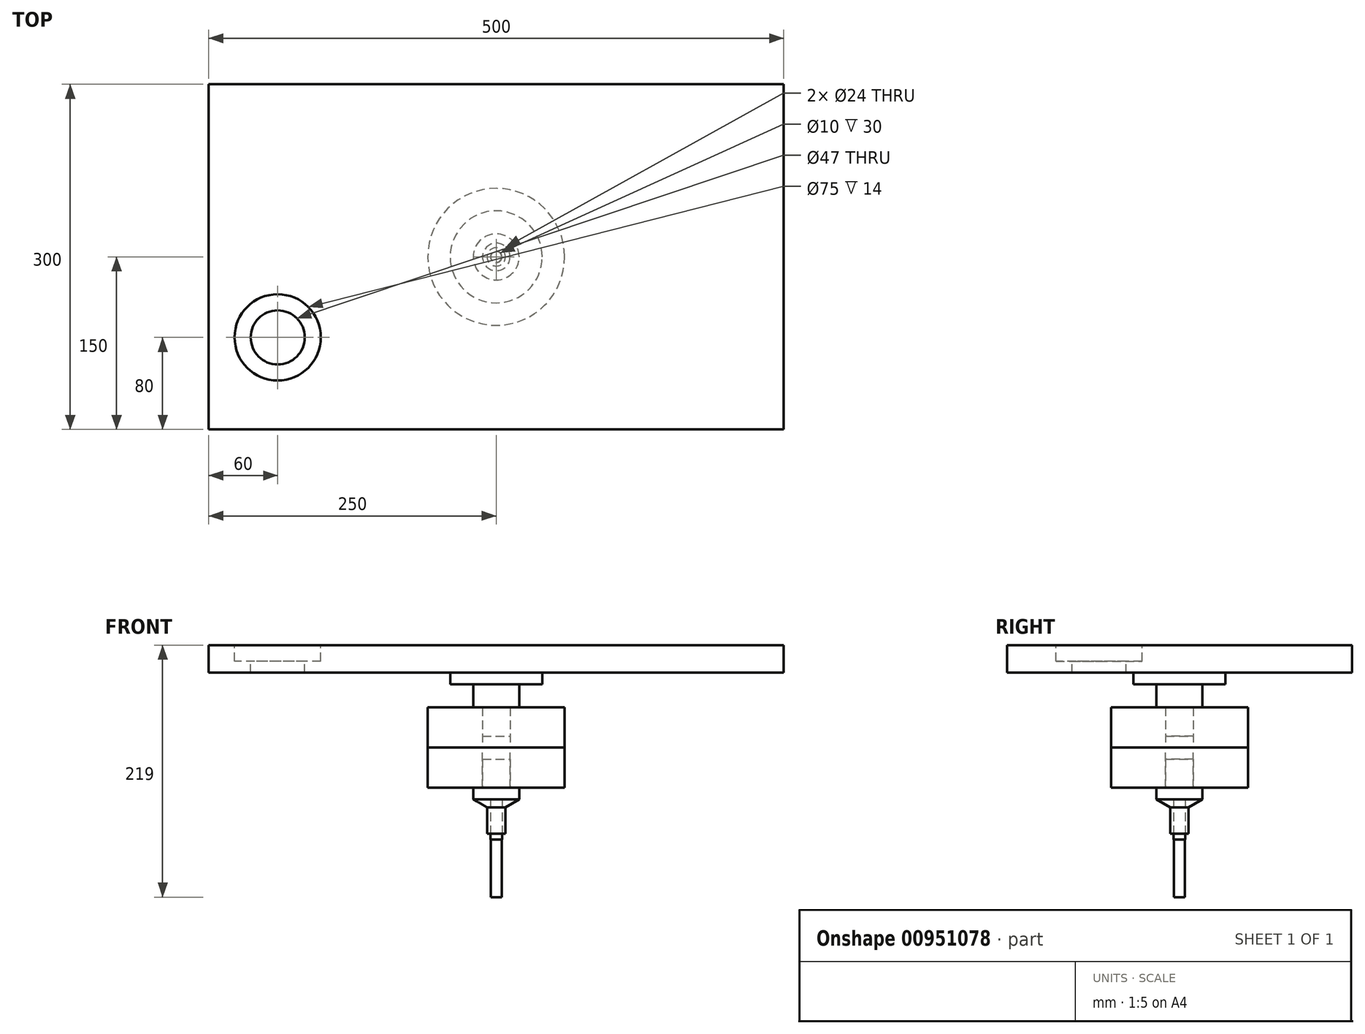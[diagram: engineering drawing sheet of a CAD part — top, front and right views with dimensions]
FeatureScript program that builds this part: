
annotation { "Feature Type Name" : "Feature", "Feature Type Description" : "" }
export const myFeature = defineFeature(function(context is Context, id is Id, definition is map)
    precondition{}
    {
        {
            var Q0;
            Q0=qCreatedBy(makeId("Top.planeOp"),FACE);
            var sketch = newSketch(context, id + "F0", { "sketchPlane" : qUnion([Q0])});
            skLineSegment(sketch, "E0.bottom", {"start": v(250, 150) * mm, "end": v(-250, 150) * mm});
            skLineSegment(sketch, "E0.top", {"start": v(250, -150) * mm, "end": v(-250, -150) * mm});
            skLineSegment(sketch, "E0.left", {"start": v(250, 150) * mm, "end": v(250, -150) * mm});
            skLineSegment(sketch, "E0.right", {"start": v(-250, 150) * mm, "end": v(-250, -150) * mm});
            skPoint(sketch, "E0.middle", {"position": v(0, 0) * mm});
            skSolve(sketch);
        }
        {
            var Q0;
            Q0=makeQuery(id+"F0.imprint","IMPRINT",FACE,{"disambiguationData":[TD([[makeQuery(id+"F0.imprint","IMPRINT",EDGE,{"derivedFrom":sQuery(id+"F0.wireOp",EDGE,"E0.bottom")}),1.0]])]});
            var Q1;
            Q1=makeQuery(id+"F0.imprint","IMPRINT",FACE,{"disambiguationData":[TD([[makeQuery(id+"F0.imprint","IMPRINT",EDGE,{"derivedFrom":sQuery(id+"F0.wireOp",EDGE,"58def0f7-d9c0-4334-95c1-cc013ec1d39d.1.0.0")}),1.0]])]});
            var Q2;
            Q2=makeQuery(id+"F0.imprint","IMPRINT",FACE,{"disambiguationData":[TD([[makeQuery(id+"F0.imprint","IMPRINT",EDGE,{"derivedFrom":sQuery(id+"F0.wireOp",EDGE,"58def0f7-d9c0-4334-95c1-cc013ec1d39d.1.0.0")}),-1.0]])]});
            var Q3;
            Q3=makeQuery(id+"F0.imprint","IMPRINT",FACE,{"disambiguationData":[TD([[makeQuery(id+"F0.imprint","IMPRINT",EDGE,{"derivedFrom":sQuery(id+"F0.wireOp",EDGE,"58def0f7-d9c0-4334-95c1-cc013ec1d39d.1.1.0")}),-1.0]])]});
            var Q4;
            Q4=makeQuery(id+"F0.imprint","IMPRINT",FACE,{"disambiguationData":[TD([[makeQuery(id+"F0.imprint","IMPRINT",EDGE,{"derivedFrom":sQuery(id+"F0.wireOp",EDGE,"58def0f7-d9c0-4334-95c1-cc013ec1d39d.1.1.0")}),1.0]])]});
            var Q5;
            Q5=makeQuery(id+"F0.imprint","IMPRINT",FACE,{"disambiguationData":[TD([[makeQuery(id+"F0.imprint","IMPRINT",EDGE,{"derivedFrom":sQuery(id+"F0.wireOp",EDGE,"58def0f7-d9c0-4334-95c1-cc013ec1d39d.0.1.0")}),-1.0]])]});
            var Q6;
            Q6=makeQuery(id+"F0.imprint","IMPRINT",FACE,{"disambiguationData":[TD([[makeQuery(id+"F0.imprint","IMPRINT",EDGE,{"derivedFrom":sQuery(id+"F0.wireOp",EDGE,"58def0f7-d9c0-4334-95c1-cc013ec1d39d.0.1.0")}),1.0]])]});
            var Q7;
            Q7=makeQuery(id+"F0.imprint","IMPRINT",FACE,{"disambiguationData":[TD([[makeQuery(id+"F0.imprint","IMPRINT",EDGE,{"derivedFrom":sQuery(id+"F0.wireOp",EDGE,"4IipATZv-LVdL-YkI8-DpBN-fSkK8KW6vcjz")}),1.0]])]});
            var Q8;
            Q8=makeQuery(id+"F0.imprint","IMPRINT",FACE,{"disambiguationData":[TD([[makeQuery(id+"F0.imprint","IMPRINT",EDGE,{"derivedFrom":sQuery(id+"F0.wireOp",EDGE,"YpDaPiLN-B9xz-3bgj-5HSM-HLz1pKYE0Ii8")}),1.0]])]});
            extrude(context, id + "F1", {"entities" : qUnion([Q0, Q1, Q2, Q3, Q4, Q5, Q6, Q7, Q8]), "depth" : 24 * mm, "offsetDistance" : 25 * mm});
        }
        {
            var Q0;
            Q0=makeQuery(id+"F1.opExtrude","CAP_FACE",FACE,{"disambiguationData":[OSD([sQuery(id+"F0.wireOp",EDGE,"E0.bottom"),sQuery(id+"F0.wireOp",EDGE,"E0.top"),sQuery(id+"F0.wireOp",EDGE,"E0.left"),sQuery(id+"F0.wireOp",EDGE,"E0.right")])],"isStart":false});
            var sketch = newSketch(context, id + "F2", { "sketchPlane" : qUnion([Q0])});
            skCircle(sketch, "E1", {"center": v(-190, -70) * mm, "radius": 37.5 * mm});
            skCircle(sketch, "E2", {"center": v(-190, -70) * mm, "radius": 23.5 * mm});
            skSolve(sketch);
        }
        {
            var Q0;
            Q0=makeQuery(id+"F2.imprint","IMPRINT",FACE,{"disambiguationData":[TD([[makeQuery(id+"F2.imprint","IMPRINT",EDGE,{"derivedFrom":sQuery(id+"F2.wireOp",EDGE,"E2")}),1.0]])]});
            extrude(context, id + "F3", {"entities" : qUnion([Q0]), "operationType" : NewBodyOperationType.REMOVE, "endBound" : BoundingType.THROUGH_ALL, "oppositeDirection" : true, "depth" : 25 * mm, "offsetDistance" : 25 * mm});
        }
        {
            var Q0;
            Q0=makeQuery(id+"F2.imprint","IMPRINT",FACE,{"disambiguationData":[TD([[makeQuery(id+"F2.imprint","IMPRINT",EDGE,{"derivedFrom":sQuery(id+"F2.wireOp",EDGE,"E1")}),1.0]])]});
            extrude(context, id + "F4", {"entities" : qUnion([Q0]), "operationType" : NewBodyOperationType.REMOVE, "oppositeDirection" : true, "depth" : 14 * mm, "offsetDistance" : 25 * mm});
        }
        {
            var Q0;
            Q0=qCreatedBy(makeId("Front.planeOp"),FACE);
            var sketch = newSketch(context, id + "F5", { "sketchPlane" : qUnion([Q0])});
            skLineSegment(sketch, "E3", {"start": v(0, -55) * mm, "end": v(0, 0) * mm});
            skLineSegment(sketch, "E4", {"start": v(0, 0) * mm, "end": v(40, 0) * mm});
            skLineSegment(sketch, "E5", {"start": v(40, 0) * mm, "end": v(40, -10) * mm});
            skLineSegment(sketch, "E6", {"start": v(12, -30) * mm, "end": v(12, -55) * mm});
            skLineSegment(sketch, "E7", {"start": v(12, -55) * mm, "end": v(0, -55) * mm});
            skLineSegment(sketch, "E8", {"start": v(12, -30) * mm, "end": v(20, -30) * mm});
            skLineSegment(sketch, "E9", {"start": v(20, -30) * mm, "end": v(20, -10) * mm});
            skLineSegment(sketch, "E10", {"start": v(20, -10) * mm, "end": v(40, -10) * mm});
            skLineSegment(sketch, "E11.MirrorCS", {"start": v(-12, -30) * mm, "end": v(-12, -55) * mm, "construction": true});
            skLineSegment(sketch, "E12.MirrorCS", {"start": v(-20, -30) * mm, "end": v(-20, -10) * mm, "construction": true});
            skLineSegment(sketch, "E13.MirrorCS", {"start": v(-40, 0) * mm, "end": v(-40, -10) * mm, "construction": true});
            skLineSegment(sketch, "E14", {"start": v(20, -30) * mm, "end": v(59.5, -30) * mm});
            skLineSegment(sketch, "E15", {"start": v(59.5, -30) * mm, "end": v(59.5, -65) * mm});
            skLineSegment(sketch, "E16", {"start": v(59.5, -65) * mm, "end": v(12, -65) * mm});
            skLineSegment(sketch, "E17", {"start": v(12, -65) * mm, "end": v(12, -55) * mm});
            skLineSegment(sketch, "E18.MirrorCS", {"start": v(-59.5, -30) * mm, "end": v(-59.5, -65) * mm, "construction": true});
            skLineSegment(sketch, "E19", {"start": v(0, -75) * mm, "end": v(12, -75) * mm});
            skLineSegment(sketch, "E20", {"start": v(12, -75) * mm, "end": v(12, -100) * mm});
            skLineSegment(sketch, "E21", {"start": v(12, -100) * mm, "end": v(20, -100) * mm});
            skLineSegment(sketch, "E22", {"start": v(20, -100) * mm, "end": v(20, -110) * mm});
            skLineSegment(sketch, "E23", {"start": v(20, -110) * mm, "end": v(8, -110) * mm});
            skLineSegment(sketch, "E24", {"start": v(8, -110) * mm, "end": v(8, -140) * mm});
            skLineSegment(sketch, "E25", {"start": v(8, -140) * mm, "end": v(5, -140) * mm});
            skLineSegment(sketch, "E26", {"start": v(5, -140) * mm, "end": v(5, -110) * mm});
            skLineSegment(sketch, "E27", {"start": v(5, -110) * mm, "end": v(0, -110) * mm});
            skLineSegment(sketch, "E28", {"start": v(0, -110) * mm, "end": v(0, -75) * mm});
            skLineSegment(sketch, "E29.MirrorCS", {"start": v(-5, -140) * mm, "end": v(-5, -110) * mm, "construction": true});
            skLineSegment(sketch, "E30.MirrorCS", {"start": v(-8, -110) * mm, "end": v(-8, -140) * mm, "construction": true});
            skLineSegment(sketch, "E31", {"start": v(5, -140) * mm, "end": v(5, -145) * mm});
            skLineSegment(sketch, "E32", {"start": v(5, -145) * mm, "end": v(4.75, -145) * mm});
            skLineSegment(sketch, "E33", {"start": v(4.75, -145) * mm, "end": v(4.75, -195) * mm});
            skLineSegment(sketch, "E34", {"start": v(4.75, -195) * mm, "end": v(0, -195) * mm});
            skLineSegment(sketch, "E35", {"start": v(0, -195) * mm, "end": v(0, -110) * mm});
            skLineSegment(sketch, "E36.MirrorCS", {"start": v(-4.75, -145) * mm, "end": v(-4.75, -195) * mm, "construction": true});
            skLineSegment(sketch, "E37", {"start": v(20, -110) * mm, "end": v(8, -116.93) * mm});
            skSolve(sketch);
        }
        {
            var Q0;
            Q0=makeQuery(id+"F5.imprint","IMPRINT",FACE,{"disambiguationData":[TD([[makeQuery(id+"F5.imprint","IMPRINT",EDGE,{"derivedFrom":sQuery(id+"F5.wireOp",EDGE,"E3")}),-1.0]])]});
            var Q1;
            Q1=sQuery(id+"F5.wireOp",EDGE,"E3");
            revolve(context, id + "F6", {"surfaceOperationType" : NewSurfaceOperationType.NEW, "entities" : qUnion([Q0]), "axis" : qUnion([Q1]), "revolveType" : RevolveType.FULL});
        }
        {
            var Q0;
            Q0=makeQuery(id+"F5.imprint","IMPRINT",FACE,{"disambiguationData":[TD([[makeQuery(id+"F5.imprint","IMPRINT",EDGE,{"derivedFrom":sQuery(id+"F5.wireOp",EDGE,"E6")}),1.0]])]});
            var Q1;
            Q1=sQuery(id+"F5.wireOp",EDGE,"E3");
            revolve(context, id + "F7", {"surfaceOperationType" : NewSurfaceOperationType.NEW, "entities" : qUnion([Q0]), "axis" : qUnion([Q1]), "revolveType" : RevolveType.FULL});
        }
        {
            var Q0;
            Q0=makeQuery(id+"F7.opRevolve","SWEPT_BODY",BODY,{"disambiguationData":[OSD([sQuery(id+"F5.wireOp",EDGE,"E6"),sQuery(id+"F5.wireOp",EDGE,"E8"),sQuery(id+"F5.wireOp",EDGE,"E14"),sQuery(id+"F5.wireOp",EDGE,"E15"),sQuery(id+"F5.wireOp",EDGE,"E16"),sQuery(id+"F5.wireOp",EDGE,"E17")])]});
            var Q1;
            Q1=makeQuery(id+"F7.opRevolve","SWEPT_FACE",FACE,{"disambiguationData":[OSD([sQuery(id+"F5.wireOp",EDGE,"E16")])]});
            mirror(context, id + "F8", {"entities" : qUnion([Q0]), "mirrorPlane" : qUnion([Q1])});
        }
        {
            var Q0;
            Q0=makeQuery(id+"F5.imprint","IMPRINT",FACE,{"disambiguationData":[TD([[makeQuery(id+"F5.imprint","IMPRINT",EDGE,{"derivedFrom":sQuery(id+"F5.wireOp",EDGE,"E19")}),-1.0]])]});
            var Q1;
            {var subQ0=sQuery(id+"F5.wireOp",EDGE,"E23");Q1=makeQuery(id+"F5.imprint","IMPRINT",FACE,{"disambiguationData":[TD([[makeQuery(id+"F5.imprint","IMPRINT",EDGE,{"derivedFrom":subQ0}),1.0]])]});}
            var Q2;
            Q2=sQuery(id+"F5.wireOp",EDGE,"E28");
            revolve(context, id + "F9", {"surfaceOperationType" : NewSurfaceOperationType.NEW, "entities" : qUnion([Q0, Q1]), "axis" : qUnion([Q2]), "revolveType" : RevolveType.FULL});
        }
        {
            var Q0;
            Q0=makeQuery(id+"F5.imprint","IMPRINT",FACE,{"disambiguationData":[TD([[makeQuery(id+"F5.imprint","IMPRINT",EDGE,{"derivedFrom":sQuery(id+"F5.wireOp",EDGE,"E26")}),1.0]])]});
            var Q1;
            Q1=sQuery(id+"F5.wireOp",EDGE,"E35");
            revolve(context, id + "F10", {"surfaceOperationType" : NewSurfaceOperationType.NEW, "entities" : qUnion([Q0]), "axis" : qUnion([Q1]), "revolveType" : RevolveType.FULL});
        }
    });
